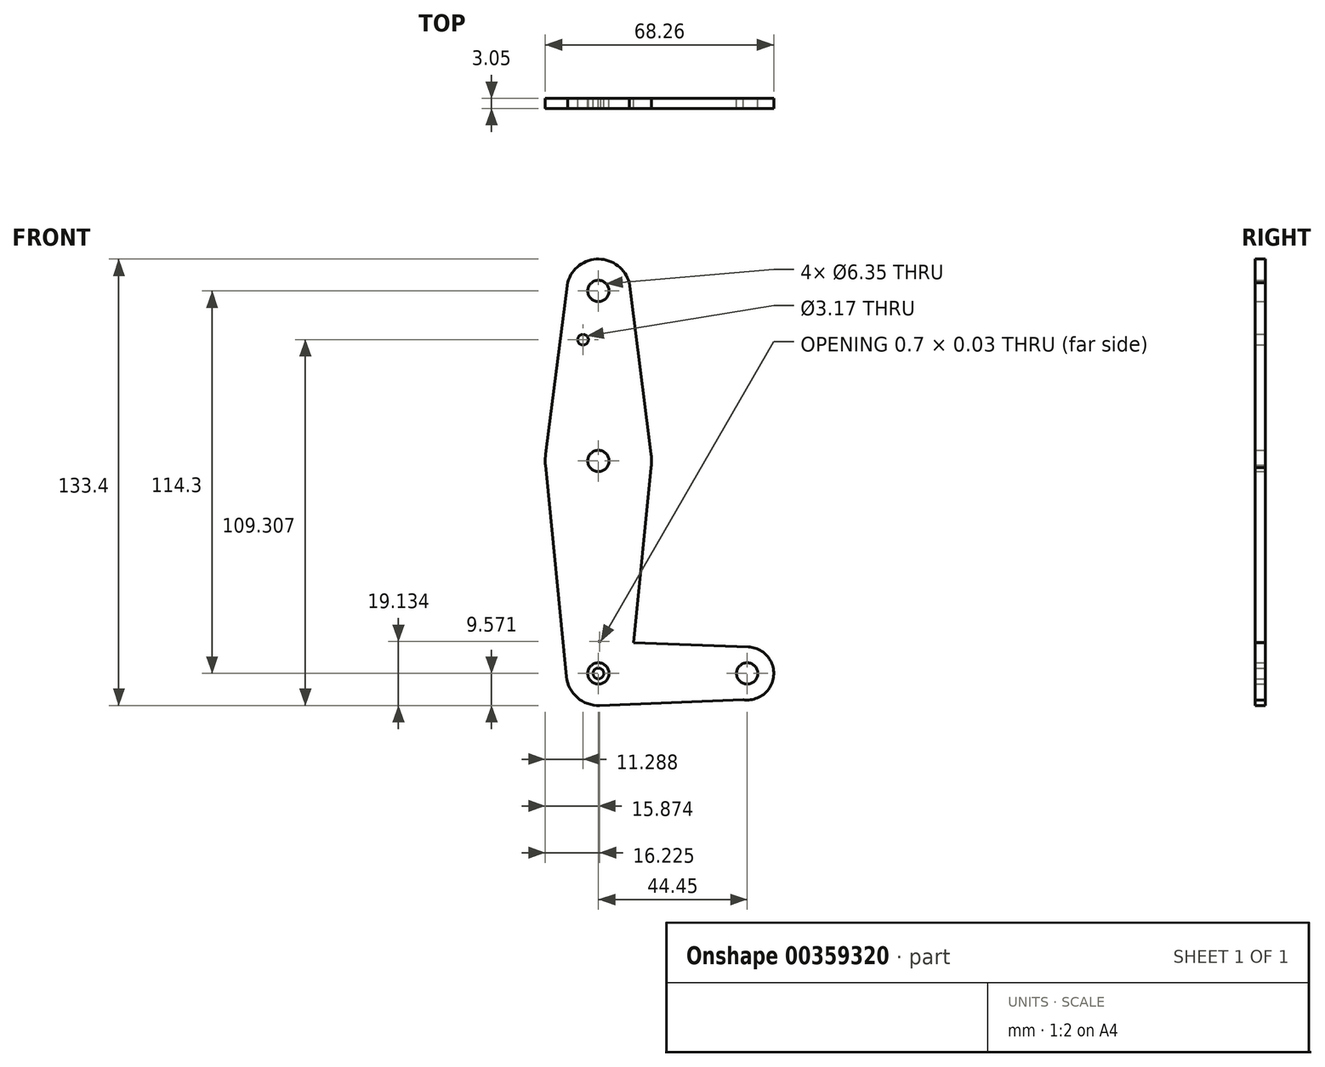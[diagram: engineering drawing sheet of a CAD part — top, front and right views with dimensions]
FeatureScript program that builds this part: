
annotation { "Feature Type Name" : "Feature", "Feature Type Description" : "" }
export const myFeature = defineFeature(function(context is Context, id is Id, definition is map)
    precondition{}
    {
        {
            var Q0;
            Q0=qCreatedBy(makeId("Front.planeOp"),FACE);
            var sketch = newSketch(context, id + "F0", { "sketchPlane" : qUnion([Q0])});
            skLineSegment(sketch, "E0", {"start": v(-35.72, 54) * mm, "end": v(-35.72, 3.2) * mm, "construction": true});
            skLineSegment(sketch, "E1", {"start": v(-35.72, 3.2) * mm, "end": v(-35.72, -60.3) * mm, "construction": true});
            skLineSegment(sketch, "E2", {"start": v(-35.72, -60.3) * mm, "end": v(8.73, -60.3) * mm, "construction": true});
            skCircle(sketch, "E3", {"center": v(-35.72, 54) * mm, "radius": 9.53 * mm});
            skCircle(sketch, "E4", {"center": v(-35.72, 3.2) * mm, "radius": 15.88 * mm});
            skCircle(sketch, "E5", {"center": v(-35.72, -60.3) * mm, "radius": 9.58 * mm});
            skCircle(sketch, "E6", {"center": v(8.73, -60.3) * mm, "radius": 7.94 * mm});
            skLineSegment(sketch, "E7", {"start": v(-44.87, 56.64) * mm, "end": v(-51.46, 5.22) * mm});
            skLineSegment(sketch, "E8", {"start": v(-51.54, 1.96) * mm, "end": v(-45.24, -61.25) * mm});
            skLineSegment(sketch, "E9", {"start": v(-26.51, 56.45) * mm, "end": v(-19.97, 5.21) * mm});
            skLineSegment(sketch, "E10", {"start": v(-19.97, 1.2) * mm, "end": v(-26.19, -61.25) * mm});
            skLineSegment(sketch, "E11", {"start": v(-35.72, -50.72) * mm, "end": v(9.03, -52.37) * mm});
            skLineSegment(sketch, "E12", {"start": v(-35.33, -69.87) * mm, "end": v(9.03, -68.1) * mm});
            skCircle(sketch, "E13", {"center": v(-35.72, 54) * mm, "radius": 3.18 * mm});
            skCircle(sketch, "E14", {"center": v(-35.72, 3.2) * mm, "radius": 3.18 * mm});
            skCircle(sketch, "E15", {"center": v(-35.72, -60.3) * mm, "radius": 3.18 * mm});
            skCircle(sketch, "E16", {"center": v(8.73, -60.3) * mm, "radius": 3.18 * mm});
            skCircle(sketch, "E17", {"center": v(-40.3, 39.44) * mm, "radius": 1.59 * mm});
            skCircle(sketch, "E18", {"center": v(-35.72, -60.3) * mm, "radius": 1.6 * mm});
            skSolve(sketch);
        }
        {
            var Q0;
            Q0=makeQuery(id+"F0.imprint","IMPRINT",FACE,{"disambiguationData":[TD([[makeQuery(id+"F0.imprint","IMPRINT",EDGE,{"derivedFrom":sQuery(id+"F0.wireOp",EDGE,"E13")}),-1.0]])]});
            var Q1;
            Q1=makeQuery(id+"F0.imprint","IMPRINT",FACE,{"disambiguationData":[TD([[makeQuery(id+"F0.imprint","IMPRINT",EDGE,{"derivedFrom":sQuery(id+"F0.wireOp",EDGE,"E17")}),-1.0]])]});
            var Q2;
            Q2=makeQuery(id+"F0.imprint","IMPRINT",FACE,{"disambiguationData":[TD([[makeQuery(id+"F0.imprint","IMPRINT",EDGE,{"derivedFrom":sQuery(id+"F0.wireOp",EDGE,"E14")}),-1.0]])]});
            var Q3;
            {var subQ5=sQuery(id+"F0.wireOp",EDGE,"E4");var subQ8=sQuery(id+"F0.wireOp",EDGE,"E10");var subQ9=makeQuery(id+"F0.imprint","INTERSECT",VERTEX,{"derivedFrom":[subQ5,subQ8]});Q3=makeQuery(id+"F0.imprint","IMPRINT",FACE,{"disambiguationData":[TD([[makeQuery(id+"F0.imprint","IMPRINT",EDGE,{"disambiguationData":[TD([[subQ9,1.0]])],"derivedFrom":subQ5}),-1.0]])]});}
            var Q4;
            Q4=makeQuery(id+"F0.imprint","IMPRINT",FACE,{"disambiguationData":[TD([[makeQuery(id+"F0.imprint","IMPRINT",EDGE,{"derivedFrom":sQuery(id+"F0.wireOp",EDGE,"E15")}),-1.0]])]});
            var Q5;
            {var subQ0=sQuery(id+"F0.wireOp",EDGE,"E10");var subQ1=sQuery(id+"F0.wireOp",EDGE,"E5");var subQ2=makeQuery(id+"F0.imprint","INTERSECT",VERTEX,{"derivedFrom":[subQ1,subQ0]});Q5=makeQuery(id+"F0.imprint","IMPRINT",FACE,{"disambiguationData":[TD([[makeQuery(id+"F0.imprint","IMPRINT",EDGE,{"disambiguationData":[TD([[subQ2,-1.0]])],"derivedFrom":subQ1}),-1.0]])]});}
            var Q6;
            {var subQ3=sQuery(id+"F0.wireOp",EDGE,"E10");var subQ5=sQuery(id+"F0.wireOp",EDGE,"E5");var subQ6=makeQuery(id+"F0.imprint","INTERSECT",VERTEX,{"derivedFrom":[subQ5,subQ3]});Q6=makeQuery(id+"F0.imprint","IMPRINT",FACE,{"disambiguationData":[TD([[makeQuery(id+"F0.imprint","IMPRINT",EDGE,{"disambiguationData":[TD([[subQ6,1.0]])],"derivedFrom":subQ5}),-1.0]])]});}
            var Q7;
            Q7=makeQuery(id+"F0.imprint","IMPRINT",FACE,{"disambiguationData":[TD([[makeQuery(id+"F0.imprint","IMPRINT",EDGE,{"derivedFrom":sQuery(id+"F0.wireOp",EDGE,"E16")}),-1.0]])]});
            var Q8;
            Q8=makeQuery(id+"F0.imprint","IMPRINT",FACE,{"disambiguationData":[TD([[makeQuery(id+"F0.imprint","IMPRINT",EDGE,{"derivedFrom":sQuery(id+"F0.wireOp",EDGE,"E18")}),1.0]])]});
            extrude(context, id + "F1", {"entities" : qUnion([Q0, Q1, Q2, Q3, Q4, Q5, Q6, Q7, Q8]), "depth" : 3.05 * mm});
        }
    });
